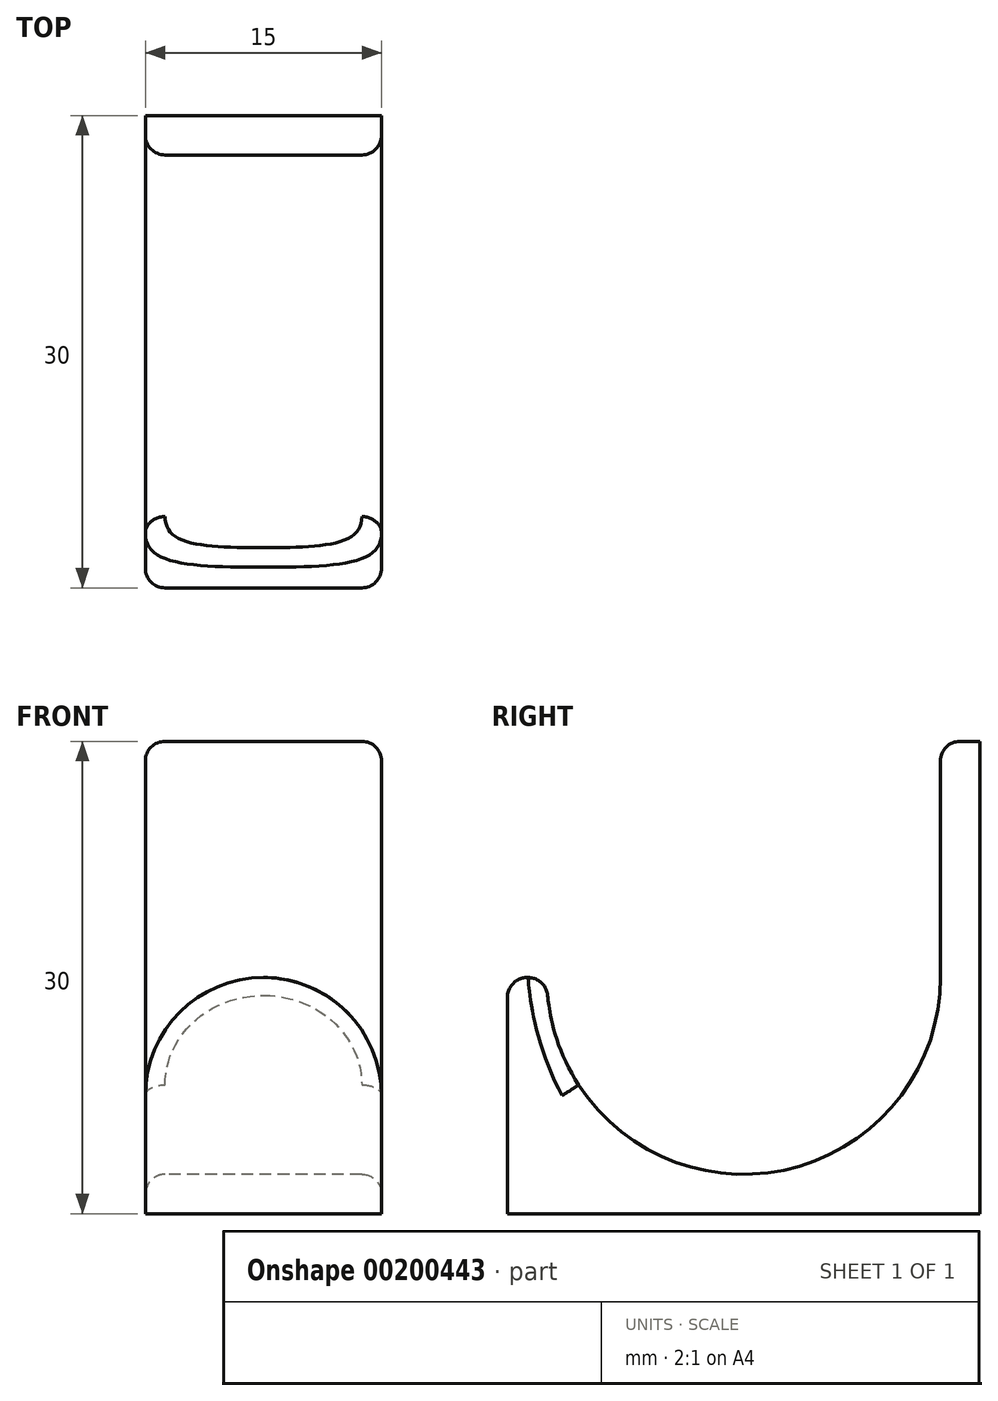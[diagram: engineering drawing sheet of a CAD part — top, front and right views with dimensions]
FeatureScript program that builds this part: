
annotation { "Feature Type Name" : "Feature", "Feature Type Description" : "" }
export const myFeature = defineFeature(function(context is Context, id is Id, definition is map)
    precondition{}
    {
        {
            var Q0;
            Q0=qCreatedBy(makeId("Right.planeOp"),FACE);
            var sketch = newSketch(context, id + "F0", { "sketchPlane" : qUnion([Q0])});
            skCircle(sketch, "E0", {"center": v(0, 15) * mm, "radius": 12.5 * mm});
            skCircle(sketch, "E1", {"center": v(0, 15) * mm, "radius": 15 * mm});
            skLineSegment(sketch, "E2", {"start": v(-15, 15) * mm, "end": v(-15, 0) * mm});
            skLineSegment(sketch, "E3", {"start": v(-15, 0) * mm, "end": v(15, 0) * mm});
            skLineSegment(sketch, "E4", {"start": v(15, 0) * mm, "end": v(15, 15) * mm});
            skLineSegment(sketch, "E5", {"start": v(0, 2.5) * mm, "end": v(15, 2.5) * mm});
            skLineSegment(sketch, "E6", {"start": v(0, 30) * mm, "end": v(0, 27.5) * mm});
            skLineSegment(sketch, "E7", {"start": v(-15, 15) * mm, "end": v(-15, 30) * mm});
            skLineSegment(sketch, "E8", {"start": v(-15, 30) * mm, "end": v(0, 30) * mm});
            skSolve(sketch);
        }
        {
            var Q0;
            {var subQ0=sQuery(id+"F0.wireOp",EDGE,"E2");Q0=makeQuery(id+"F0.imprint","IMPRINT",FACE,{"disambiguationData":[TD([[makeQuery(id+"F0.imprint","IMPRINT",EDGE,{"derivedFrom":subQ0}),1.0]])]});}
            var Q1;
            {var subQ0=sQuery(id+"F0.wireOp",EDGE,"E3");var subQ1=sQuery(id+"F0.wireOp",EDGE,"E1");var subQ2=makeQuery(id+"F0.imprint","INTERSECT",VERTEX,{"derivedFrom":[subQ1,subQ0]});Q1=makeQuery(id+"F0.imprint","IMPRINT",FACE,{"disambiguationData":[TD([[makeQuery(id+"F0.imprint","IMPRINT",EDGE,{"disambiguationData":[TD([[subQ2,-1.0]])],"derivedFrom":subQ1}),-1.0]])]});}
            var Q2;
            {var subQ7=sQuery(id+"F0.wireOp",EDGE,"E6");Q2=makeQuery(id+"F0.imprint","IMPRINT",FACE,{"disambiguationData":[TD([[makeQuery(id+"F0.imprint","IMPRINT",EDGE,{"derivedFrom":subQ7}),-1.0]])]});}
            var Q3;
            {var subQ0=sQuery(id+"F0.wireOp",EDGE,"E7");Q3=makeQuery(id+"F0.imprint","IMPRINT",FACE,{"disambiguationData":[TD([[makeQuery(id+"F0.imprint","IMPRINT",EDGE,{"derivedFrom":subQ0}),-1.0]])]});}
            extrude(context, id + "F1", {"entities" : qUnion([Q0, Q1, Q2, Q3]), "endBound" : BoundingType.SYMMETRIC, "depth" : 15 * mm});
        }
        {
            var Q0;
            Q0=makeQuery(id+"F1.opExtrude","CAP_EDGE",EDGE,{"disambiguationData":[OSD([sQuery(id+"F0.wireOp",EDGE,"E6")])],"isStart":false});
            var Q1;
            Q1=makeQuery(id+"F1.opExtrude","CAP_EDGE",EDGE,{"disambiguationData":[OSD([sQuery(id+"F0.wireOp",EDGE,"E6")])],"isStart":true});
            fillet(context, id + "F2", {"entities" : qUnion([Q0, Q1]), "radius" : 7.5 * mm, "tangentPropagation" : true, "allowEdgeOverflow" : false});
        }
        {
            var Q0;
            Q0=makeQuery(id+"F1.opExtrude","CAP_EDGE",EDGE,{"disambiguationData":[OSD([sQuery(id+"F0.wireOp",EDGE,"E0")])],"isStart":false});
            var Q1;
            Q1=makeQuery(id+"F1.opExtrude","CAP_EDGE",EDGE,{"disambiguationData":[OSD([sQuery(id+"F0.wireOp",EDGE,"E8")])],"isStart":false});
            var Q2;
            Q2=makeQuery(id+"F1.opExtrude","CAP_EDGE",EDGE,{"disambiguationData":[OSD([sQuery(id+"F0.wireOp",EDGE,"E4")])],"isStart":false});
            var Q3;
            Q3=makeQuery(id+"F1.opExtrude","CAP_EDGE",EDGE,{"disambiguationData":[OSD([sQuery(id+"F0.wireOp",EDGE,"E4")])],"isStart":true});
            var Q4;
            Q4=makeQuery(id+"F1.opExtrude","SWEPT_EDGE",EDGE,{"disambiguationData":[OSD([sQuery(id+"F0.wireOp",EDGE,"E4"),sQuery(id+"F0.wireOp",EDGE,"E5")])]});
            fillet(context, id + "F3", {"entities" : qUnion([Q0, Q1, Q2, Q3, Q4]), "radius" : 1.25 * mm, "tangentPropagation" : true, "allowEdgeOverflow" : false});
        }
        {
            var Q0;
            Q0=qCreatedBy(makeId("Front.planeOp"),FACE);
            var sketch = newSketch(context, id + "F4", { "sketchPlane" : qUnion([Q0])});
            skLineSegment(sketch, "E9", {"start": v(-31.89, 15) * mm, "end": v(39.08, 15) * mm, "construction": true});
            skSolve(sketch);
        }
        {
            var Q0;
            Q0=makeQuery(id+"F1.opExtrude","SWEPT_BODY",BODY,{"disambiguationData":[OSD([sQuery(id+"F0.wireOp",EDGE,"E0"),sQuery(id+"F0.wireOp",EDGE,"E2"),sQuery(id+"F0.wireOp",EDGE,"E3"),sQuery(id+"F0.wireOp",EDGE,"E4"),sQuery(id+"F0.wireOp",EDGE,"E5"),sQuery(id+"F0.wireOp",EDGE,"E6"),sQuery(id+"F0.wireOp",EDGE,"E7"),sQuery(id+"F0.wireOp",EDGE,"E8")])]});
            var Q1;
            Q1=sQuery(id+"F4.wireOp",EDGE,"E9");
            transform(context, id + "F5", {"entities" : qUnion([Q0]), "transformType" : TransformType.ROTATION, "transformAxis" : qUnion([Q1]), "angle" : 90 * degree, "makeCopy" : false});
        }
    });
